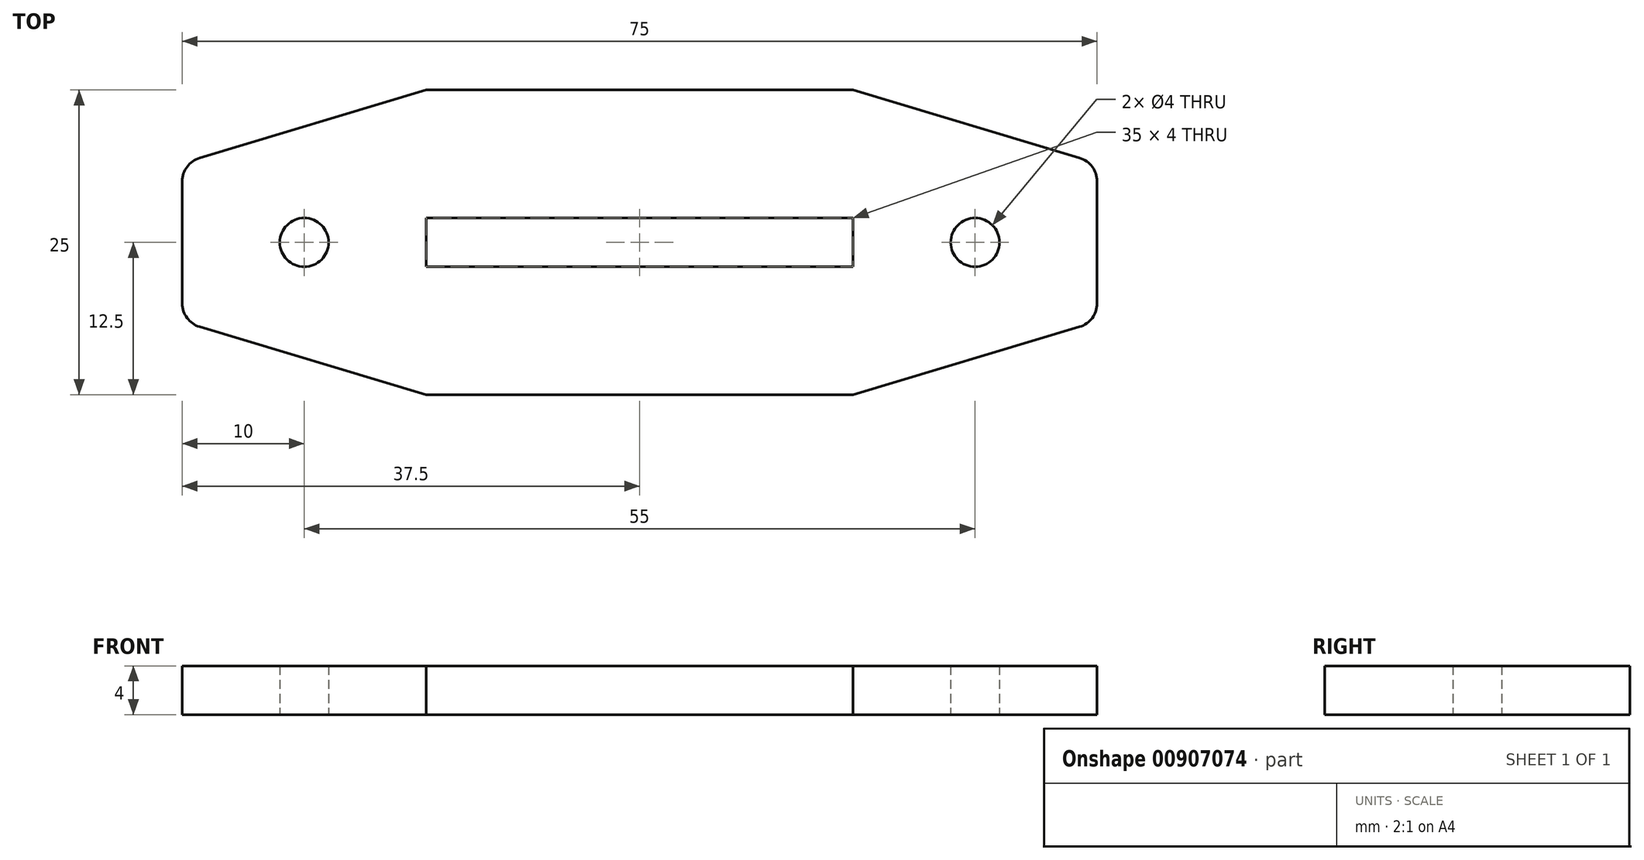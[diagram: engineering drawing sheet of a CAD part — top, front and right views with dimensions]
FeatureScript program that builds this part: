
annotation { "Feature Type Name" : "Feature", "Feature Type Description" : "" }
export const myFeature = defineFeature(function(context is Context, id is Id, definition is map)
    precondition{}
    {
        {
            var Q0;
            Q0=qCreatedBy(makeId("Top.planeOp"),FACE);
            var sketch = newSketch(context, id + "F0", { "sketchPlane" : qUnion([Q0])});
            skLineSegment(sketch, "E0.bottom", {"start": v(0, 12.5) * mm, "end": v(-17.5, 12.5) * mm});
            skLineSegment(sketch, "E0.top", {"start": v(0, -12.5) * mm, "end": v(-17.5, -12.5) * mm});
            skLineSegment(sketch, "E0.right", {"start": v(-37.5, 6.5) * mm, "end": v(-37.5, -6.5) * mm});
            skPoint(sketch, "E0.middle", {"position": v(0, 0) * mm});
            skLineSegment(sketch, "E1", {"start": v(-37.5, 6.5) * mm, "end": v(-17.5, 12.5) * mm});
            skLineSegment(sketch, "E2", {"start": v(-37.5, -6.5) * mm, "end": v(-17.5, -12.5) * mm});
            skLineSegment(sketch, "E3", {"start": v(0, 12.5) * mm, "end": v(0, -12.5) * mm, "construction": true});
            skPoint(sketch, "E4.orphan", {"position": v(-37.5, 12.5) * mm});
            skPoint(sketch, "E5.orphan", {"position": v(-37.5, -12.5) * mm});
            skPoint(sketch, "E0.left.end.orphan", {"position": v(37.5, -12.5) * mm});
            skPoint(sketch, "E0.left.start.orphan", {"position": v(37.5, 12.5) * mm});
            skLineSegment(sketch, "E6.MirrorCS", {"start": v(0, 12.5) * mm, "end": v(17.5, 12.5) * mm});
            skLineSegment(sketch, "E7.MirrorCS", {"start": v(37.5, 6.5) * mm, "end": v(17.5, 12.5) * mm});
            skLineSegment(sketch, "E8.MirrorCS", {"start": v(37.5, 6.5) * mm, "end": v(37.5, -6.5) * mm});
            skLineSegment(sketch, "E9.MirrorCS", {"start": v(37.5, -6.5) * mm, "end": v(17.5, -12.5) * mm});
            skLineSegment(sketch, "E10.MirrorCS", {"start": v(0, -12.5) * mm, "end": v(17.5, -12.5) * mm});
            skLineSegment(sketch, "E11.bottom", {"start": v(17.5, 2) * mm, "end": v(-17.5, 2) * mm});
            skLineSegment(sketch, "E11.top", {"start": v(17.5, -2) * mm, "end": v(-17.5, -2) * mm});
            skLineSegment(sketch, "E11.left", {"start": v(17.5, 2) * mm, "end": v(17.5, -2) * mm});
            skLineSegment(sketch, "E11.right", {"start": v(-17.5, 2) * mm, "end": v(-17.5, -2) * mm});
            skCircle(sketch, "E12", {"center": v(-27.5, 0) * mm, "radius": 2 * mm});
            skCircle(sketch, "E13", {"center": v(27.5, 0) * mm, "radius": 2 * mm});
            skLineSegment(sketch, "E14", {"start": v(-37.5, 0) * mm, "end": v(37.5, 0) * mm, "construction": true});
            skSolve(sketch);
        }
        {
            var Q0;
            Q0 = qSketchRegion(id + "F0", true);
            extrude(context, id + "F1", {"entities" : qUnion([Q0]), "depth" : 4 * mm, "offsetDistance" : 25 * mm});
        }
        {
            var Q0;
            Q0=makeQuery(id+"F1.opExtrude","SWEPT_EDGE",EDGE,{"disambiguationData":[OSD([sQuery(id+"F0.wireOp",EDGE,"E0.right"),sQuery(id+"F0.wireOp",EDGE,"E2")])]});
            var Q1;
            Q1=makeQuery(id+"F1.opExtrude","SWEPT_EDGE",EDGE,{"disambiguationData":[OSD([sQuery(id+"F0.wireOp",EDGE,"E8.MirrorCS"),sQuery(id+"F0.wireOp",EDGE,"E9.MirrorCS")])]});
            var Q2;
            Q2=makeQuery(id+"F1.opExtrude","SWEPT_EDGE",EDGE,{"disambiguationData":[OSD([sQuery(id+"F0.wireOp",EDGE,"E7.MirrorCS"),sQuery(id+"F0.wireOp",EDGE,"E8.MirrorCS")])]});
            var Q3;
            Q3=makeQuery(id+"F1.opExtrude","SWEPT_EDGE",EDGE,{"disambiguationData":[OSD([sQuery(id+"F0.wireOp",EDGE,"E0.right"),sQuery(id+"F0.wireOp",EDGE,"E1")])]});
            fillet(context, id + "F2", {"entities" : qUnion([Q0, Q1, Q2, Q3]), "radius" : 2 * mm, "tangentPropagation" : true, "allowEdgeOverflow" : false});
        }
    });
